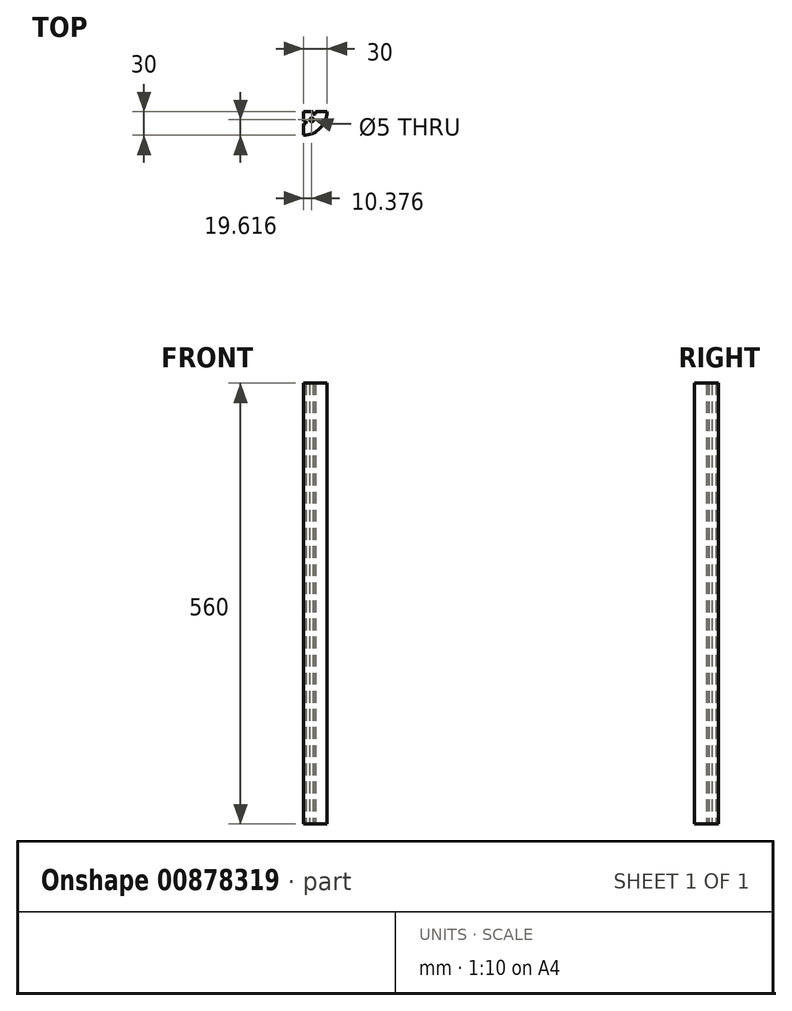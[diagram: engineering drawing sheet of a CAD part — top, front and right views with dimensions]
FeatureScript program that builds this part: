
annotation { "Feature Type Name" : "Feature", "Feature Type Description" : "" }
export const myFeature = defineFeature(function(context is Context, id is Id, definition is map)
    precondition{}
    {
        {
            var Q0;
            Q0=qCreatedBy(makeId("Top.planeOp"),FACE);
            var sketch = newSketch(context, id + "F0", { "sketchPlane" : qUnion([Q0])});
            skLineSegment(sketch, "E0.bottom", {"start": v(-52.64, -50.16) * mm, "end": v(-40.64, -50.16) * mm});
            skLineSegment(sketch, "E0.left", {"start": v(-52.64, -50.16) * mm, "end": v(-52.64, -62.16) * mm});
            skArc(sketch, "E1", {"start": v(-52.64, -80.16) * mm, "mid": v(-31.43, -71.38) * mm, "end": v(-22.64, -50.16) * mm});
            skCircle(sketch, "E2", {"center": v(-42.26, -60.54) * mm, "radius": 2.5 * mm});
            skLineSegment(sketch, "E3.top", {"start": v(-37.64, -53.16) * mm, "end": v(-40.64, -53.16) * mm});
            skLineSegment(sketch, "E3.left", {"start": v(-37.64, -50.16) * mm, "end": v(-37.64, -53.16) * mm});
            skLineSegment(sketch, "E3.right", {"start": v(-40.64, -50.16) * mm, "end": v(-40.64, -53.16) * mm});
            skLineSegment(sketch, "E4.bottom", {"start": v(-52.64, -65.16) * mm, "end": v(-49.64, -65.16) * mm});
            skLineSegment(sketch, "E4.top", {"start": v(-52.64, -62.16) * mm, "end": v(-49.64, -62.16) * mm});
            skLineSegment(sketch, "E4.right", {"start": v(-49.64, -65.16) * mm, "end": v(-49.64, -62.16) * mm});
            skLineSegment(sketch, "E5.trimOffspring", {"start": v(-52.64, -65.16) * mm, "end": v(-52.64, -80.16) * mm});
            skLineSegment(sketch, "E6.trimOffspring", {"start": v(-37.64, -50.16) * mm, "end": v(-22.64, -50.16) * mm});
            skSolve(sketch);
        }
        {
            var Q0;
            Q0=makeQuery(id+"F0.imprint","IMPRINT",FACE,{"disambiguationData":[TD([[makeQuery(id+"F0.imprint","IMPRINT",EDGE,{"derivedFrom":sQuery(id+"F0.wireOp",EDGE,"E0.bottom")}),-1.0]])]});
            extrude(context, id + "F1", {"entities" : qUnion([Q0]), "depth" : 560 * mm, "offsetDistance" : 25 * mm});
        }
    });
